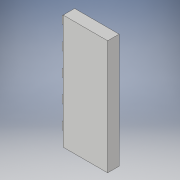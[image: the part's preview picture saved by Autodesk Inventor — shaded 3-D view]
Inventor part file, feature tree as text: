
AUTODESK INVENTOR PART (.ipt)
format: ipt  version: 2017 (Build 210142000, 142)  size: 157,696 bytes
history: native  units: in
note: dims shown in document units (in); Inventor stores cm internally (conversion verified against a paired STEP export)
features: extrude x3, sketch x2
ambient origin geometry x8: Origin, YZ Plane, XZ Plane, XY Plane, X Axis, Y Axis, Z Axis, Center Point
bodies: Solid1 (feature_tree)
feature tree (5):
  extrude  "door"  Depth=9.0in
  sketch  "Sketch2"  dims[d2=0.9in d3=0.0in d19=0.7in d20=0.0in d21=0.7in d22=0.0in d36=0.25in d37=9.0in d38=0.45in d39=0.45in d40=0.45in d41=0.45in d42=0.45in d43=0.45in d44=0.45in d45=0.45in d46=45.0deg d47=45.0deg d48=0.45in]
  extrude  "teeth cut"  Depth=0.7in TaperAngle=0.0deg
  extrude  "teeth make"  Depth=0.7in
  sketch  "Sketch1"  dims[d0=3.5in d1=9.0in]
